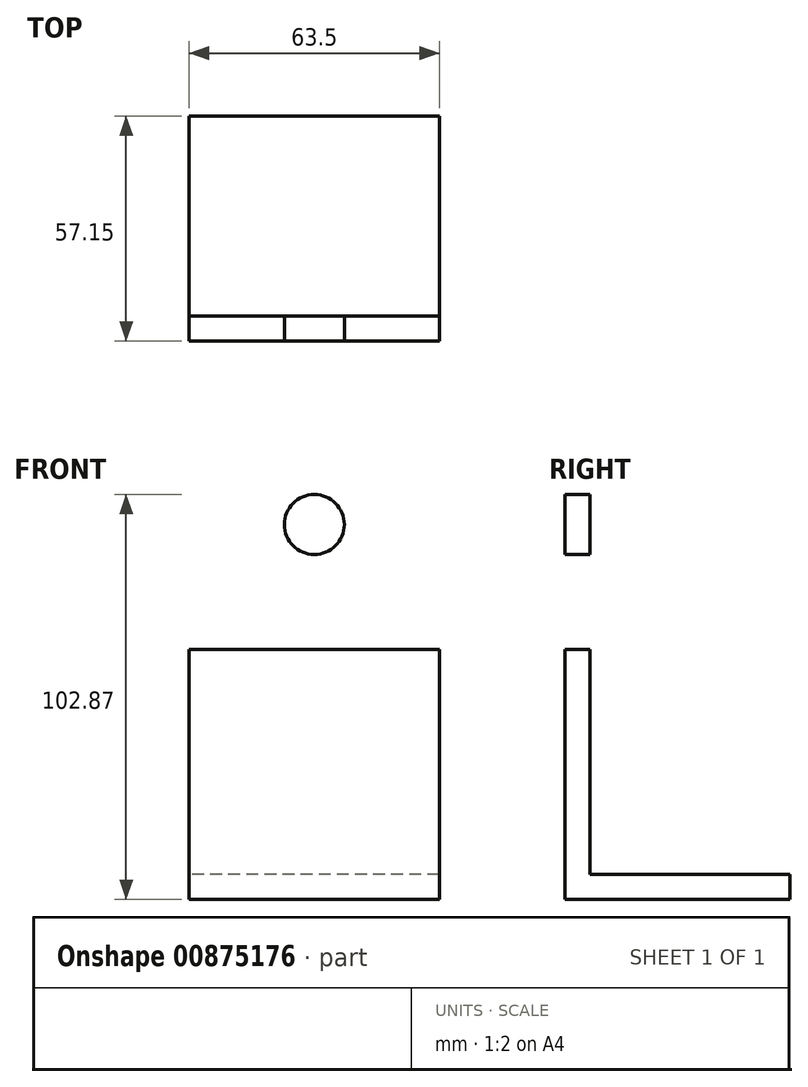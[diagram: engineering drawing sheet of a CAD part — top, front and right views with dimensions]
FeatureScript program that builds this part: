
annotation { "Feature Type Name" : "Feature", "Feature Type Description" : "" }
export const myFeature = defineFeature(function(context is Context, id is Id, definition is map)
    precondition{}
    {
        {
            var Q0;
            Q0=qCreatedBy(makeId("Front.planeOp"),FACE);
            var sketch = newSketch(context, id + "F0", { "sketchPlane" : qUnion([Q0])});
            skLineSegment(sketch, "E0.bottom", {"start": v(-137.53, 117) * mm, "end": v(-74.03, 117) * mm});
            skLineSegment(sketch, "E0.top", {"start": v(-137.53, -10) * mm, "end": v(-74.03, -10) * mm});
            skLineSegment(sketch, "E0.left", {"start": v(-137.53, 117) * mm, "end": v(-137.53, -10) * mm});
            skLineSegment(sketch, "E0.right", {"start": v(-74.03, 117) * mm, "end": v(-74.03, -10) * mm});
            skSolve(sketch);
        }
        {
            var Q0;
            Q0=makeQuery(id+"F0.imprint","IMPRINT",FACE,{"disambiguationData":[TD([[makeQuery(id+"F0.imprint","IMPRINT",EDGE,{"derivedFrom":sQuery(id+"F0.wireOp",EDGE,"E0.bottom")}),-1.0]])]});
            extrude(context, id + "F1", {"entities" : qUnion([Q0]), "depth" : 6.35 * mm, "offsetDistance" : 25.4 * mm});
        }
        {
            var Q0;
            Q0=makeQuery(id+"F1.opExtrude","CAP_FACE",FACE,{"disambiguationData":[OSD([sQuery(id+"F0.wireOp",EDGE,"E0.bottom"),sQuery(id+"F0.wireOp",EDGE,"E0.top"),sQuery(id+"F0.wireOp",EDGE,"E0.left"),sQuery(id+"F0.wireOp",EDGE,"E0.right")])],"isStart":true});
            var sketch = newSketch(context, id + "F2", { "sketchPlane" : qUnion([Q0])});
            skLineSegment(sketch, "E1.bottom", {"start": v(74.03, -10) * mm, "end": v(137.53, -10) * mm});
            skLineSegment(sketch, "E1.top", {"start": v(74.03, -3.64) * mm, "end": v(137.53, -3.64) * mm});
            skLineSegment(sketch, "E1.left", {"start": v(74.03, -10) * mm, "end": v(74.03, -3.64) * mm});
            skLineSegment(sketch, "E1.right", {"start": v(137.53, -10) * mm, "end": v(137.53, -3.64) * mm});
            skSolve(sketch);
        }
        {
            var Q0;
            Q0=makeQuery(id+"F2.imprint","IMPRINT",FACE,{"disambiguationData":[TD([[makeQuery(id+"F2.imprint","IMPRINT",EDGE,{"derivedFrom":sQuery(id+"F2.wireOp",EDGE,"E1.bottom")}),-1.0]])]});
            extrude(context, id + "F3", {"entities" : qUnion([Q0]), "operationType" : NewBodyOperationType.ADD, "depth" : 50.8 * mm, "offsetDistance" : 25.4 * mm});
        }
        {
            var Q0;
            Q0=makeQuery(id+"F1.opExtrude","CAP_FACE",FACE,{"disambiguationData":[OSD([sQuery(id+"F0.wireOp",EDGE,"E0.bottom"),sQuery(id+"F0.wireOp",EDGE,"E0.top"),sQuery(id+"F0.wireOp",EDGE,"E0.left"),sQuery(id+"F0.wireOp",EDGE,"E0.right")])],"isStart":false});
            var sketch = newSketch(context, id + "F4", { "sketchPlane" : qUnion([Q0])});
            skLineSegment(sketch, "E2.bottom", {"start": v(-137.53, 117) * mm, "end": v(-74.03, 117) * mm});
            skLineSegment(sketch, "E2.top", {"start": v(-137.53, 53.5) * mm, "end": v(-74.03, 53.5) * mm});
            skLineSegment(sketch, "E2.left", {"start": v(-137.53, 117) * mm, "end": v(-137.53, 53.5) * mm});
            skLineSegment(sketch, "E2.right", {"start": v(-74.03, 117) * mm, "end": v(-74.03, 53.5) * mm});
            skLineSegment(sketch, "E3", {"start": v(-137.53, 117) * mm, "end": v(-105.78, 117) * mm});
            skLineSegment(sketch, "E4", {"start": v(-105.78, 117) * mm, "end": v(-105.78, 53.5) * mm});
            skCircle(sketch, "E5", {"center": v(-105.78, 85.26) * mm, "radius": 7.62 * mm});
            skSolve(sketch);
        }
        {
            var Q0;
            {var subQ0=sQuery(id+"F4.wireOp",EDGE,"E5");var subQ1=sQuery(id+"F4.wireOp",EDGE,"E4");var subQ2=makeQuery(id+"F4.imprint","INTERSECT",VERTEX,{"disambiguationData":[OD(0.0)],"derivedFrom":[subQ1,subQ0]});Q0=makeQuery(id+"F4.imprint","IMPRINT",FACE,{"disambiguationData":[TD([[makeQuery(id+"F4.imprint","IMPRINT",EDGE,{"disambiguationData":[TD([[subQ2,-1.0]])],"derivedFrom":subQ1}),-1.0]])]});}
            var Q1;
            {var subQ0=sQuery(id+"F4.wireOp",EDGE,"E5");var subQ1=sQuery(id+"F4.wireOp",EDGE,"E4");var subQ2=makeQuery(id+"F4.imprint","INTERSECT",VERTEX,{"disambiguationData":[OD(0.0)],"derivedFrom":[subQ1,subQ0]});Q1=makeQuery(id+"F4.imprint","IMPRINT",FACE,{"disambiguationData":[TD([[makeQuery(id+"F4.imprint","IMPRINT",EDGE,{"disambiguationData":[TD([[subQ2,-1.0]])],"derivedFrom":subQ1}),1.0]])]});}
            extrude(context, id + "F5", {"entities" : qUnion([Q0, Q1]), "operationType" : NewBodyOperationType.REMOVE, "oppositeDirection" : true, "depth" : 25.4 * mm, "offsetDistance" : 25.4 * mm});
        }
    });
